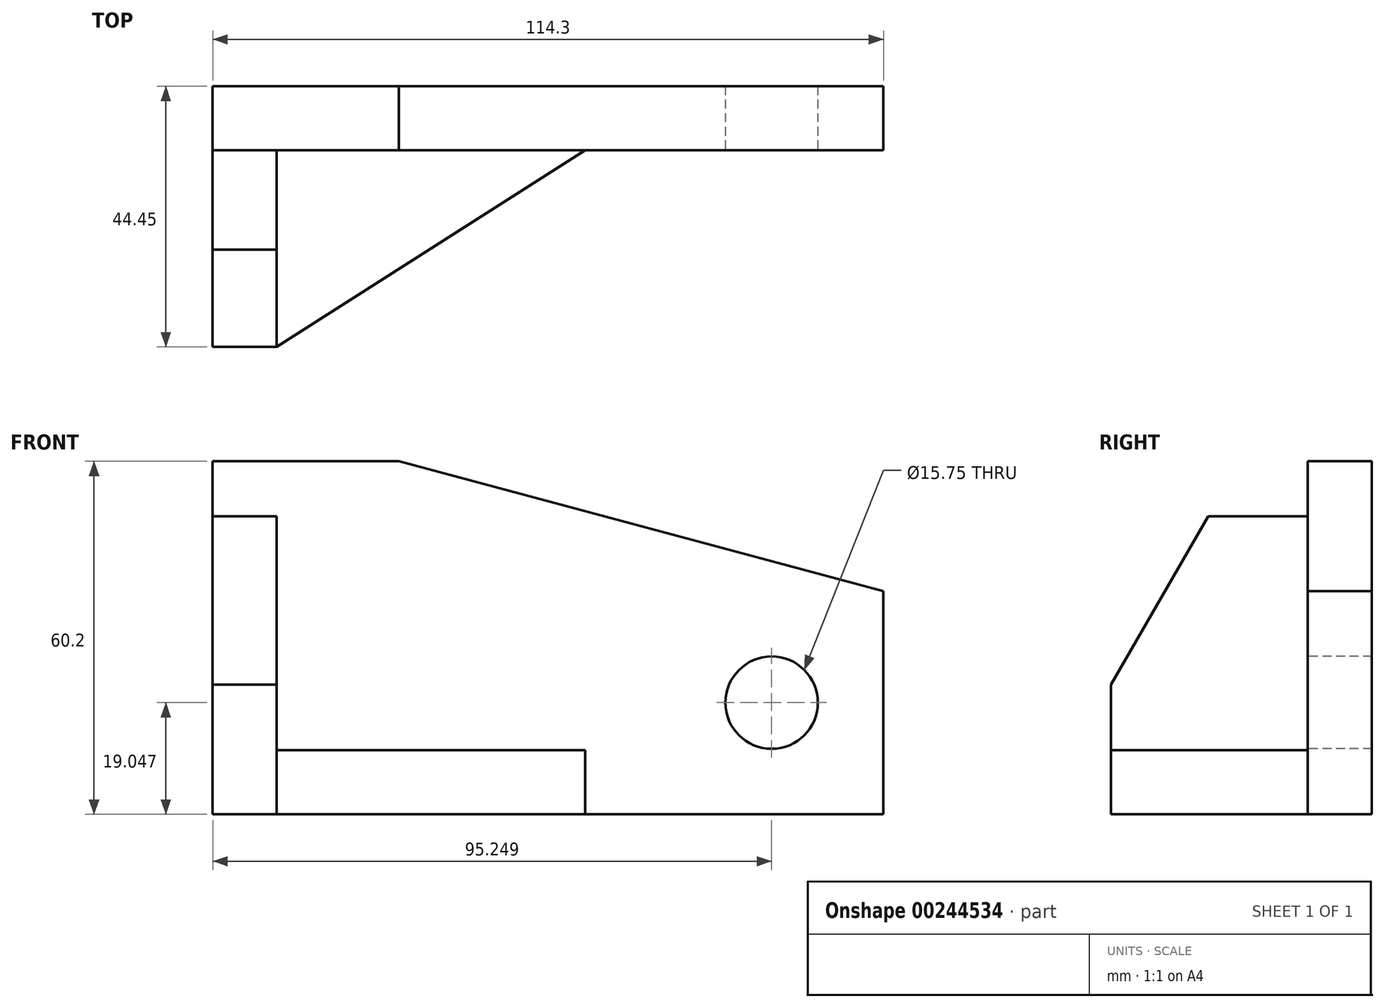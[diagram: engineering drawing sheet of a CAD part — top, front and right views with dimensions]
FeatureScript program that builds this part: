
annotation { "Feature Type Name" : "Feature", "Feature Type Description" : "" }
export const myFeature = defineFeature(function(context is Context, id is Id, definition is map)
    precondition{}
    {
        {
            var Q0;
            Q0=qCreatedBy(makeId("Front.planeOp"),FACE);
            var sketch = newSketch(context, id + "F0", { "sketchPlane" : qUnion([Q0])});
            skLineSegment(sketch, "E0", {"start": v(-35.6, 24.62) * mm, "end": v(-67.34, 24.62) * mm});
            skLineSegment(sketch, "E1", {"start": v(-67.34, 24.62) * mm, "end": v(-67.34, -35.58) * mm});
            skLineSegment(sketch, "E2", {"start": v(-67.34, -35.58) * mm, "end": v(46.96, -35.58) * mm});
            skLineSegment(sketch, "E3", {"start": v(46.96, -35.58) * mm, "end": v(46.96, 2.5) * mm});
            skLineSegment(sketch, "E4", {"start": v(46.96, 2.5) * mm, "end": v(-35.6, 24.62) * mm});
            skLineSegment(sketch, "E5", {"start": v(-35.6, 24.62) * mm, "end": v(46.96, 24.62) * mm});
            skLineSegment(sketch, "E6", {"start": v(46.96, 24.62) * mm, "end": v(46.96, 2.5) * mm});
            skSolve(sketch);
        }
        {
            var Q0;
            Q0=makeQuery(id+"F0.imprint","IMPRINT",FACE,{"disambiguationData":[TD([[makeQuery(id+"F0.imprint","IMPRINT",EDGE,{"derivedFrom":sQuery(id+"F0.wireOp",EDGE,"E0")}),1.0]])]});
            extrude(context, id + "F1", {"entities" : qUnion([Q0]), "depth" : 10.92 * mm});
        }
        {
            var Q0;
            Q0=makeQuery(id+"F1.opExtrude","CAP_FACE",FACE,{"disambiguationData":[OSD([sQuery(id+"F0.wireOp",EDGE,"E0"),sQuery(id+"F0.wireOp",EDGE,"E1"),sQuery(id+"F0.wireOp",EDGE,"E2"),sQuery(id+"F0.wireOp",EDGE,"E3"),sQuery(id+"F0.wireOp",EDGE,"E4")])],"isStart":false});
            var sketch = newSketch(context, id + "F2", { "sketchPlane" : qUnion([Q0])});
            skLineSegment(sketch, "E7", {"start": v(-67.34, 15.22) * mm, "end": v(-56.42, 15.22) * mm});
            skLineSegment(sketch, "E8", {"start": v(-56.42, 15.22) * mm, "end": v(-56.42, -24.66) * mm});
            skLineSegment(sketch, "E9", {"start": v(-56.42, -24.66) * mm, "end": v(-3.84, -24.66) * mm});
            skLineSegment(sketch, "E10", {"start": v(-3.84, -24.66) * mm, "end": v(-3.84, -35.58) * mm});
            skSolve(sketch);
        }
        {
            var Q0;
            {var subQ4=sQuery(id+"F2.wireOp",EDGE,"E7");Q0=makeQuery(id+"F2.imprint","IMPRINT",FACE,{"disambiguationData":[TD([[makeQuery(id+"F2.imprint","IMPRINT",EDGE,{"derivedFrom":subQ4}),-1.0]])]});}
            extrude(context, id + "F3", {"entities" : qUnion([Q0]), "operationType" : NewBodyOperationType.ADD, "depth" : 33.53 * mm});
        }
        {
            var Q0;
            Q0=makeQuery(id+"F3.opExtrude","SWEPT_FACE",FACE,{"disambiguationData":[OSD([sQuery(id+"F2.wireOp",EDGE,"E8")])]});
            var sketch = newSketch(context, id + "F4", { "sketchPlane" : qUnion([Q0])});
            skLineSegment(sketch, "E11", {"start": v(-36.94, -24.66) * mm, "end": v(-36.94, -13.48) * mm});
            skLineSegment(sketch, "E12", {"start": v(-36.94, -13.48) * mm, "end": v(-44.45, -13.48) * mm});
            skLineSegment(sketch, "E13", {"start": v(-44.45, -13.48) * mm, "end": v(-27.88, 15.22) * mm});
            skSolve(sketch);
        }
        {
            var Q0;
            {var subQ0=sQuery(id+"F4.wireOp",EDGE,"E13");Q0=makeQuery(id+"F4.imprint","IMPRINT",FACE,{"disambiguationData":[TD([[makeQuery(id+"F4.imprint","IMPRINT",EDGE,{"derivedFrom":subQ0}),1.0]])]});}
            extrude(context, id + "F5", {"entities" : qUnion([Q0]), "operationType" : NewBodyOperationType.REMOVE, "endBound" : BoundingType.THROUGH_ALL, "oppositeDirection" : true, "depth" : 25.4 * mm});
        }
        {
            var Q0;
            Q0=makeQuery(id+"F3.opExtrude","SWEPT_FACE",FACE,{"disambiguationData":[OSD([sQuery(id+"F2.wireOp",EDGE,"E9")])]});
            var sketch = newSketch(context, id + "F6", { "sketchPlane" : qUnion([Q0])});
            skLineSegment(sketch, "E14", {"start": v(-56.42, -44.45) * mm, "end": v(-3.84, -10.92) * mm});
            skSolve(sketch);
        }
        {
            var Q0;
            Q0=makeQuery(id+"F6.imprint","IMPRINT",FACE,{"disambiguationData":[TD([[makeQuery(id+"F6.imprint","IMPRINT",EDGE,{"derivedFrom":sQuery(id+"F6.wireOp",EDGE,"E14")}),-1.0]])]});
            extrude(context, id + "F7", {"entities" : qUnion([Q0]), "operationType" : NewBodyOperationType.REMOVE, "endBound" : BoundingType.THROUGH_ALL, "oppositeDirection" : true, "depth" : 25.4 * mm});
        }
        {
            var Q0;
            Q0=makeQuery(id+"F1.opExtrude","CAP_FACE",FACE,{"disambiguationData":[OSD([sQuery(id+"F0.wireOp",EDGE,"E0"),sQuery(id+"F0.wireOp",EDGE,"E1"),sQuery(id+"F0.wireOp",EDGE,"E2"),sQuery(id+"F0.wireOp",EDGE,"E3"),sQuery(id+"F0.wireOp",EDGE,"E4")])],"isStart":false});
            var sketch = newSketch(context, id + "F8", { "sketchPlane" : qUnion([Q0])});
            skLineSegment(sketch, "E15", {"start": v(27.9, -35.58) * mm, "end": v(27.9, -16.53) * mm});
            skLineSegment(sketch, "E16", {"start": v(27.9, -16.53) * mm, "end": v(46.96, -16.53) * mm});
            skCircle(sketch, "E17", {"center": v(27.9, -16.53) * mm, "radius": 7.87 * mm});
            skSolve(sketch);
        }
        {
            var Q0;
            {var subQ0=sQuery(id+"F8.wireOp",EDGE,"E16");var subQ1=sQuery(id+"F8.wireOp",EDGE,"E15");var subQ2=makeQuery(id+"F8.imprint","INTERSECT",VERTEX,{"derivedFrom":[subQ1,subQ0]});Q0=makeQuery(id+"F8.imprint","IMPRINT",FACE,{"disambiguationData":[TD([[makeQuery(id+"F8.imprint","IMPRINT",EDGE,{"disambiguationData":[TD([[subQ2,1.0]])],"derivedFrom":subQ1}),1.0]])]});}
            var Q1;
            {var subQ0=sQuery(id+"F8.wireOp",EDGE,"E16");var subQ1=sQuery(id+"F8.wireOp",EDGE,"E15");var subQ2=makeQuery(id+"F8.imprint","INTERSECT",VERTEX,{"derivedFrom":[subQ1,subQ0]});Q1=makeQuery(id+"F8.imprint","IMPRINT",FACE,{"disambiguationData":[TD([[makeQuery(id+"F8.imprint","IMPRINT",EDGE,{"disambiguationData":[TD([[subQ2,1.0]])],"derivedFrom":subQ1}),-1.0]])]});}
            extrude(context, id + "F9", {"entities" : qUnion([Q0, Q1]), "operationType" : NewBodyOperationType.REMOVE, "endBound" : BoundingType.THROUGH_ALL, "oppositeDirection" : true, "depth" : 25.4 * mm});
        }
    });
